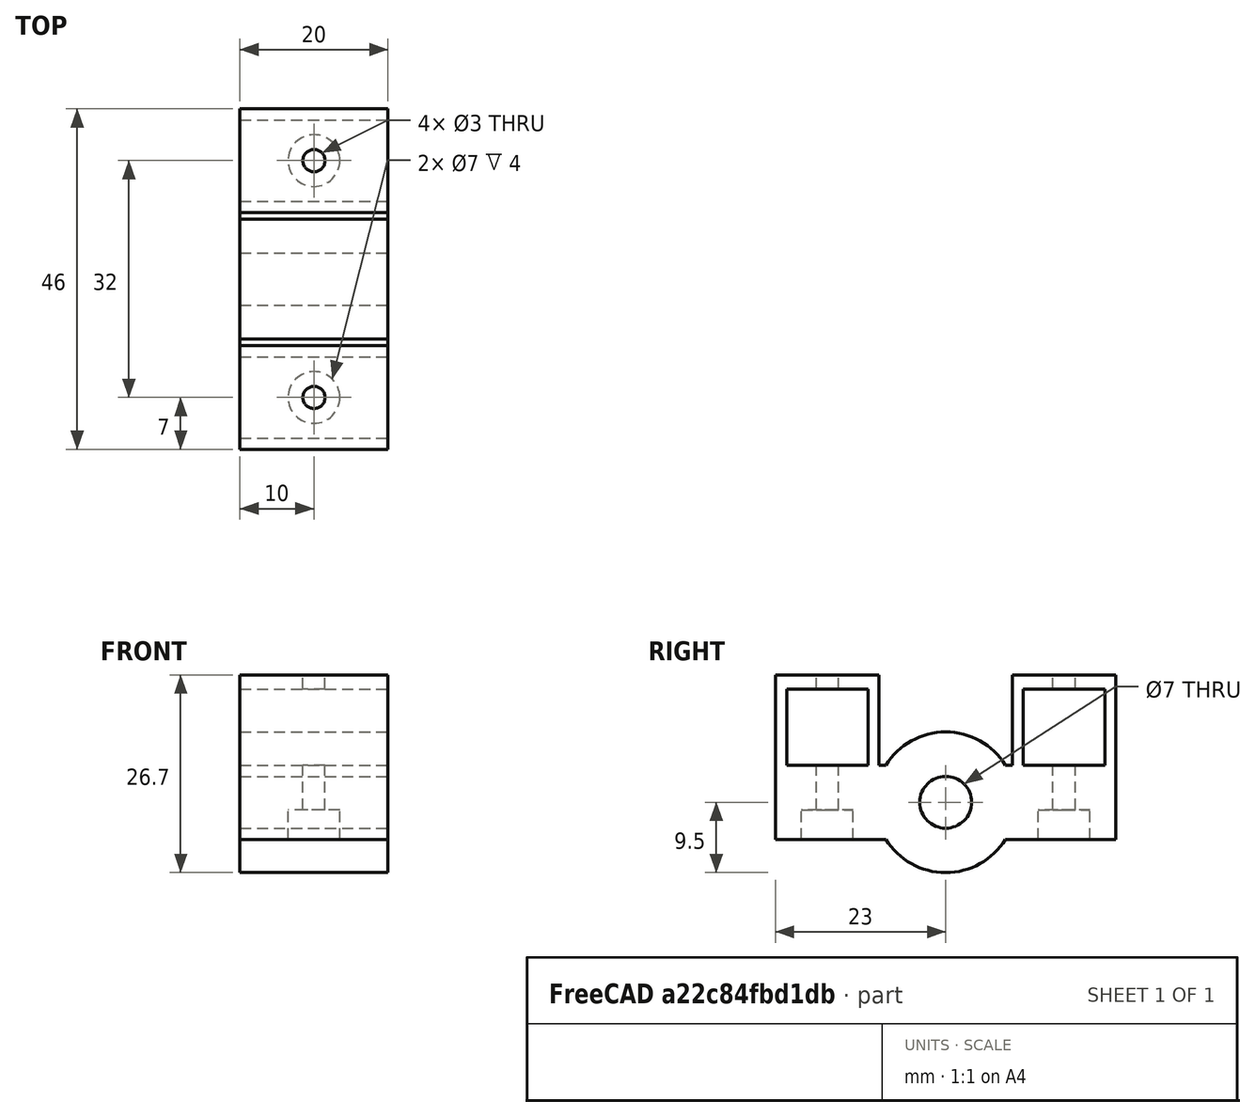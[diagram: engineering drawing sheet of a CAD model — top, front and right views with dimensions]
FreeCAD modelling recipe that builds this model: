
FCSTD DOCUMENT  (FreeCAD 0.18R16146 (Git))
Label: belt_tensioner
License: All rights reserved
LicenseURL: http://en.wikipedia.org/wiki/All_rights_reserved
objects: Part::MultiFuse×7, Part::Cylinder×6, Part::Box×5, Part::Cut×3
note: 21 computed .brp shape members not serialized (recipe doc carries the construction recipe); baked Part::Feature solids carry a one-line shape summary decoded from their .brp

FEATURE [Part::Box] Box026  label="Würfel026"
  AttacherType = Attacher::AttachEngine3D
  Height = 10
  Length = 20
  Placement = pos=(-23,-23,58) rot=(0,0,1;0rad)
  Width = 46
FEATURE [Part::Cylinder] Cylinder094  label="Zylinder091"
  Angle = 360
  AttacherType = Attacher::AttachEngine3D
  Height = 20
  Placement = pos=(-23,0,63) rot=(0,1,0;1.5708rad)
  Radius = 9.5
FEATURE [Part::Box] Box027  label="Würfel027"
  AttacherType = Attacher::AttachEngine3D
  Height = 12.2
  Length = 20
  Placement = pos=(-23,9,68) rot=(0,0,1;0rad)
  Width = 14
FEATURE [Part::Box] Box028  label="Würfel028"
  AttacherType = Attacher::AttachEngine3D
  Height = 12.2
  Length = 20
  Placement = pos=(-23,-23,68) rot=(0,0,1;0rad)
  Width = 14
FEATURE [Part::Cylinder] Cylinder097  label="Zylinder094"
  Angle = 360
  AttacherType = Attacher::AttachEngine3D
  Height = 4
  Radius = 3.5
FEATURE [Part::Cylinder] Cylinder098  label="Zylinder095"
  Angle = 360
  AttacherType = Attacher::AttachEngine3D
  Height = 25
  Radius = 1.5
FEATURE [Part::MultiFuse] Fusion034
  Placement = pos=(-13,16,58) rot=(0,0,1;0rad)
  Shapes = -> [Cylinder098,Cylinder097]
FEATURE [Part::Box] Box029  label="Würfel029"
  AttacherType = Attacher::AttachEngine3D
  Height = 10.3
  Length = 20
  Placement = pos=(-23,10.5,68) rot=(0,0,1;0rad)
  Width = 11
FEATURE [Part::Cylinder] Cylinder095  label="Zylinder092"
  Angle = 360
  AttacherType = Attacher::AttachEngine3D
  Height = 25
  Radius = 1.5
FEATURE [Part::Cylinder] Cylinder096  label="Zylinder093"
  Angle = 360
  AttacherType = Attacher::AttachEngine3D
  Height = 4
  Radius = 3.5
FEATURE [Part::MultiFuse] Fusion033
  Placement = pos=(-13,-16,58) rot=(0,0,1;0rad)
  Shapes = -> [Cylinder095,Cylinder096]
FEATURE [Part::MultiFuse] Fusion035
  Shapes = -> [Fusion033,Fusion034]
FEATURE [Part::Box] Box030  label="Würfel030"
  AttacherType = Attacher::AttachEngine3D
  Height = 10.3
  Length = 20
  Placement = pos=(-23,-21.5,68) rot=(0,0,1;0rad)
  Width = 11
FEATURE [Part::MultiFuse] Fusion030
  Shapes = -> [Box029,Box030]
FEATURE [Part::Cylinder] Cylinder093  label="Zylinder090"
  Angle = 360
  AttacherType = Attacher::AttachEngine3D
  Height = 20
  Placement = pos=(-23,0,63) rot=(0,1,0;1.5708rad)
  Radius = 3.5
FEATURE [Part::MultiFuse] Fusion029
  Shapes = -> [Box028,Box027]
FEATURE [Part::Cut] Cut047
  Base = -> Fusion029
  Tool = -> Fusion030
FEATURE [Part::MultiFuse] Fusion031
  Shapes = -> [Box026,Cut047]
FEATURE [Part::MultiFuse] Fusion032
  Shapes = -> [Cylinder094,Fusion031]
FEATURE [Part::Cut] Cut048
  Base = -> Fusion032
  Tool = -> Cylinder093
FEATURE [Part::Cut] Cut049  label="belt_tensioner"
  Base = -> Cut048
  Tool = -> Fusion035
